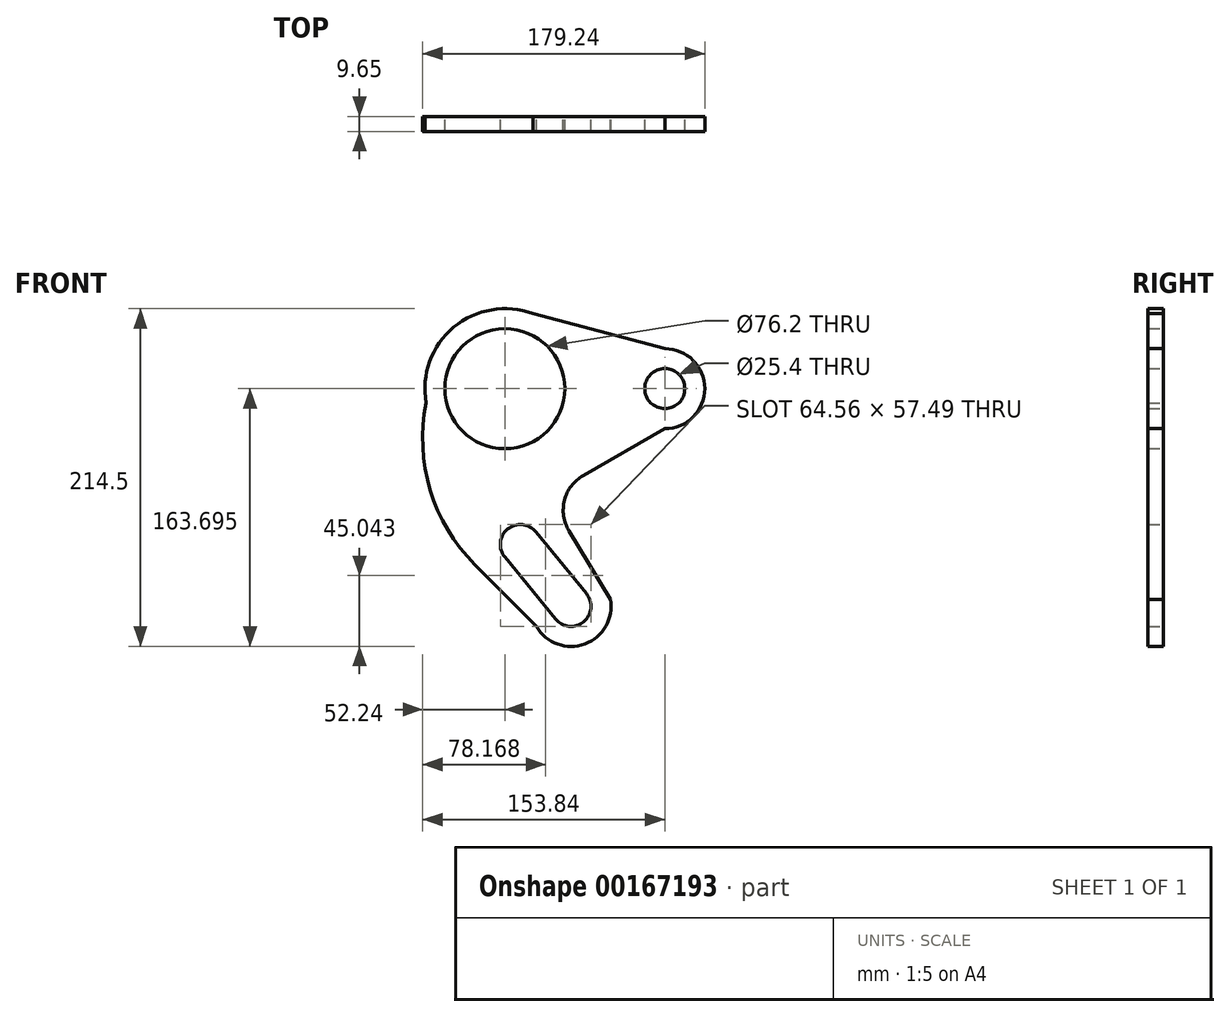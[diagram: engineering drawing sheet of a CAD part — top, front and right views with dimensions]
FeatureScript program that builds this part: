
annotation { "Feature Type Name" : "Feature", "Feature Type Description" : "" }
export const myFeature = defineFeature(function(context is Context, id is Id, definition is map)
    precondition{}
    {
        {
            var Q0;
            Q0=qCreatedBy(makeId("Front.planeOp"),FACE);
            var sketch = newSketch(context, id + "F0", { "sketchPlane" : qUnion([Q0])});
            skLineSegment(sketch, "E0", {"start": v(0, 0) * mm, "end": v(0, 44.45) * mm});
            skLineSegment(sketch, "E1", {"start": v(0, 44.45) * mm, "end": v(19.25, 33.34) * mm});
            skLineSegment(sketch, "E2", {"start": v(19.25, 33.34) * mm, "end": v(19.25, 11.11) * mm});
            skLineSegment(sketch, "E3", {"start": v(19.25, 11.11) * mm, "end": v(0, 0) * mm});
            skLineSegment(sketch, "E4", {"start": v(0, 0) * mm, "end": v(-19.25, 11.11) * mm});
            skLineSegment(sketch, "E5", {"start": v(-19.25, 11.11) * mm, "end": v(-19.25, 33.34) * mm});
            skLineSegment(sketch, "E6", {"start": v(-19.25, 33.34) * mm, "end": v(0, 44.45) * mm});
            skCircle(sketch, "E7", {"center": v(0, 22.23) * mm, "radius": 38.1 * mm});
            skCircle(sketch, "E8", {"center": v(0, 22.23) * mm, "radius": 50.8 * mm});
            skLineSegment(sketch, "E9", {"start": v(0, 22.23) * mm, "end": v(101.6, 22.23) * mm});
            skCircle(sketch, "E10", {"center": v(101.6, 22.23) * mm, "radius": 12.7 * mm});
            skLineSegment(sketch, "E11", {"start": v(101.6, 22.23) * mm, "end": v(114.3, 22.23) * mm});
            skLineSegment(sketch, "E12", {"start": v(114.3, 22.23) * mm, "end": v(127, 22.23) * mm});
            skLineSegment(sketch, "E13", {"start": v(101.6, 22.23) * mm, "end": v(101.6, 47.63) * mm});
            skLineSegment(sketch, "E14", {"start": v(101.6, 22.23) * mm, "end": v(101.6, -3.17) * mm});
            skArc(sketch, "E15", {"start": v(127, 22.23) * mm, "mid": v(119.56, 40.19) * mm, "end": v(101.6, 47.63) * mm});
            skArc(sketch, "E16", {"start": v(101.6, -3.17) * mm, "mid": v(119.56, 4.26) * mm, "end": v(127, 22.23) * mm});
            skLineSegment(sketch, "E17", {"start": v(101.6, 47.63) * mm, "end": v(8.02, 72.39) * mm});
            skLineSegment(sketch, "E18", {"start": v(101.6, -3.17) * mm, "end": v(49.81, -32.93) * mm});
            skArc(sketch, "E19", {"start": v(49.81, -32.93) * mm, "mid": v(37.87, -48.61) * mm, "end": v(40.74, -68.1) * mm});
            skLineSegment(sketch, "E20", {"start": v(40.74, -68.1) * mm, "end": v(67.03, -111.57) * mm});
            skArc(sketch, "E21", {"start": v(20.15, -128.95) * mm, "mid": v(50.86, -139.88) * mm, "end": v(67.03, -111.57) * mm});
            skLineSegment(sketch, "E22", {"start": v(20.15, -128.95) * mm, "end": v(-18.99, -89.71) * mm});
            skArc(sketch, "E23", {"start": v(-50, 13.2) * mm, "mid": v(-47.4, -42.14) * mm, "end": v(-18.99, -89.71) * mm});
            skLineSegment(sketch, "E24", {"start": v(42.04, -116.07) * mm, "end": v(9.82, -76.79) * mm});
            skLineSegment(sketch, "E25", {"start": v(9.82, -76.79) * mm, "end": v(19.64, -68.73) * mm});
            skLineSegment(sketch, "E26", {"start": v(9.82, -76.79) * mm, "end": v(0, -84.84) * mm});
            skLineSegment(sketch, "E27", {"start": v(42.04, -116.07) * mm, "end": v(51.86, -108.01) * mm});
            skLineSegment(sketch, "E28", {"start": v(42.04, -116.07) * mm, "end": v(32.22, -124.12) * mm});
            skLineSegment(sketch, "E29", {"start": v(19.64, -68.73) * mm, "end": v(51.86, -108.01) * mm});
            skLineSegment(sketch, "E30", {"start": v(0, -84.84) * mm, "end": v(32.22, -124.12) * mm});
            skArc(sketch, "E31", {"start": v(19.64, -68.73) * mm, "mid": v(1.77, -66.97) * mm, "end": v(0, -84.84) * mm});
            skArc(sketch, "E32", {"start": v(32.22, -124.12) * mm, "mid": v(50.09, -125.89) * mm, "end": v(51.86, -108.01) * mm});
            skSolve(sketch);
        }
        {
            var Q0;
            Q0 = qSketchRegion(id + "F0", true);
            extrude(context, id + "F1", {"entities" : qUnion([Q0]), "depth" : 9.65 * mm});
        }
    });
